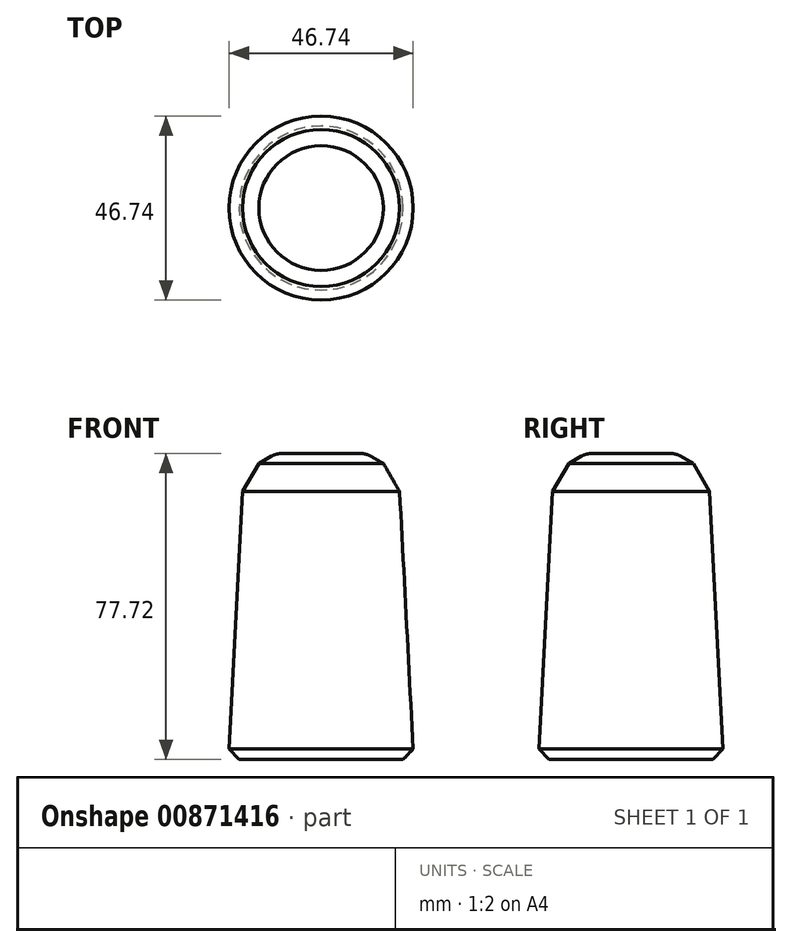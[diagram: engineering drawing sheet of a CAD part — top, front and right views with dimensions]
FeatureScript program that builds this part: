
annotation { "Feature Type Name" : "Feature", "Feature Type Description" : "" }
export const myFeature = defineFeature(function(context is Context, id is Id, definition is map)
    precondition{}
    {
        {
            var Q0;
            Q0=qCreatedBy(makeId("Top.planeOp"),FACE);
            var sketch = newSketch(context, id + "F0", { "sketchPlane" : qUnion([Q0])});
            skCircle(sketch, "E0", {"center": v(0, 0) * mm, "radius": 23.51 * mm});
            skSolve(sketch);
        }
        {
            var Q0;
            Q0=makeQuery(id+"F0.imprint","IMPRINT",FACE,{"disambiguationData":[TD([[makeQuery(id+"F0.imprint","IMPRINT",EDGE,{"derivedFrom":sQuery(id+"F0.wireOp",EDGE,"E0")}),1.0]])]});
            extrude(context, id + "F1", {"entities" : qUnion([Q0]), "depth" : 77.72 * mm, "offsetDistance" : 25.4 * mm, "hasDraft" : true, "draftAngle" : 3 * degree, "draftPullDirection" : true});
        }
        {
            var Q0;
            Q0=makeQuery(id+"F1.opExtrude","CAP_EDGE",EDGE,{"disambiguationData":[OSD([sQuery(id+"F0.wireOp",EDGE,"E0")])],"isStart":false});
            chamfer(context, id + "F2", {"entities" : qUnion([Q0]), "chamferType" : ChamferType.OFFSET_ANGLE, "width" : 5.08 * mm, "oppositeDirection" : false, "angle" : 60 * degree, "tangentPropagation" : true});
        }
        {
            var Q0;
            {var subQ0=sQuery(id+"F0.wireOp",EDGE,"E0");Q0=makeQuery(id+"F2.opChamfer","BLEND_EDGE",EDGE,{"blendedFrom":[makeQuery(id+"F1.opExtrude","CAP_EDGE",EDGE,{"disambiguationData":[OSD([subQ0])],"isStart":false}),makeQuery(id+"F1.opExtrude","CAP_FACE",FACE,{"disambiguationData":[OSD([subQ0])],"isStart":false})],"blendedInto":[makeQuery(id+"F1.opExtrude","CAP_FACE",FACE,{"disambiguationData":[OSD([subQ0])],"isStart":false})]});}
            chamfer(context, id + "F3", {"entities" : qUnion([Q0]), "width" : 5.08 * mm, "tangentPropagation" : true});
        }
        {
            var Q0;
            {var subQ0=sQuery(id+"F0.wireOp",EDGE,"E0");var subQ1=makeQuery(id+"F1.opExtrude","CAP_FACE",FACE,{"disambiguationData":[OSD([subQ0])],"isStart":false});Q0=makeQuery(id+"F3.opChamfer","BLEND_EDGE",EDGE,{"blendedFrom":[makeQuery(id+"F2.opChamfer","BLEND_EDGE",EDGE,{"blendedFrom":[makeQuery(id+"F1.opExtrude","CAP_EDGE",EDGE,{"disambiguationData":[OSD([subQ0])],"isStart":false}),subQ1],"blendedInto":[subQ1]}),subQ1],"blendedInto":[subQ1]});}
            fillet(context, id + "F4", {"entities" : qUnion([Q0]), "radius" : 5.08 * mm, "tangentPropagation" : true, "allowEdgeOverflow" : false});
        }
        {
            var Q0;
            Q0=makeQuery(id+"F1.opExtrude","CAP_EDGE",EDGE,{"disambiguationData":[OSD([sQuery(id+"F0.wireOp",EDGE,"E0")])],"isStart":true});
            chamfer(context, id + "F5", {"entities" : qUnion([Q0]), "width" : 2.54 * mm, "tangentPropagation" : true});
        }
    });
